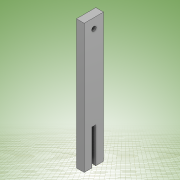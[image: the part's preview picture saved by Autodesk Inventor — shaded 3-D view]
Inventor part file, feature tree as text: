
AUTODESK INVENTOR PART (.ipt)
format: ipt  version: 2022 (Build 260153000, 153)  size: 129,536 bytes
history: native  units: mm
features: other x1, extrude x1, sketch x1
ambient origin geometry x8: Origin, YZ Plane, XZ Plane, XY Plane, X Axis, Y Axis, Z Axis, Center Point
bodies: Body1 (feature_tree)
feature tree (3):
  other  "Sólido1"
  extrude  "Extrusión1"  Depth=55.0mm
  sketch  "Boceto2"  dims[d2=7.0mm d3=15.0mm d4=12.0mm d5=0.0mm d7=6.0mm d8=30.0mm d9=12.0mm d10=200.0mm d11=12.0mm d12=55.0mm]
